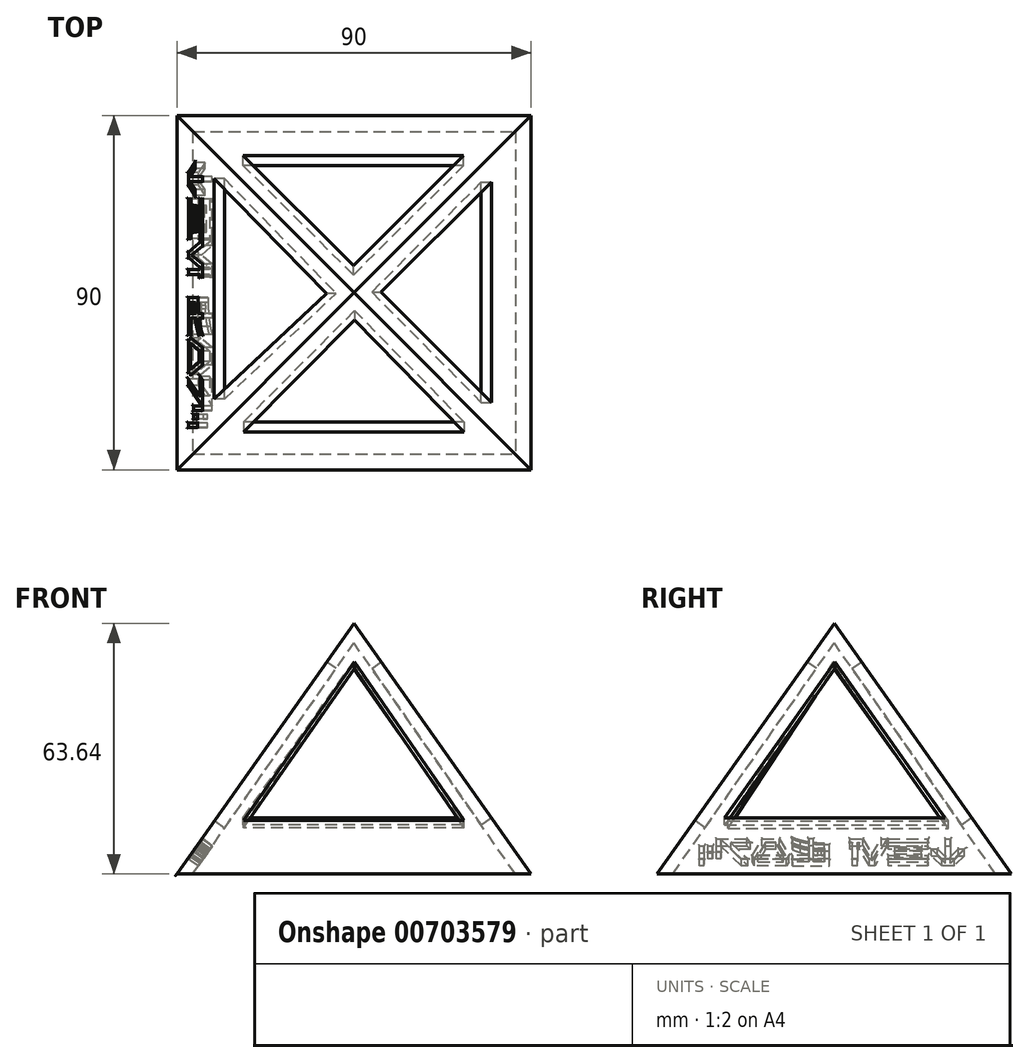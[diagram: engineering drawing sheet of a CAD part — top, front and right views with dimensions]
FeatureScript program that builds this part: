
annotation { "Feature Type Name" : "Feature", "Feature Type Description" : "" }
export const myFeature = defineFeature(function(context is Context, id is Id, definition is map)
    precondition{}
    {
        {
            var Q0;
            Q0=qCreatedBy(makeId("Top.planeOp"),FACE);
            cPlane(context, id + "F0", {"entities" : qUnion([Q0]), "cplaneType" : CPlaneType.OFFSET, "offset" : 63.64 * mm, "width" : 150 * mm, "height" : 150 * mm});
        }
        {
            var Q0;
            Q0=qCreatedBy(id+"F0.planeOp",FACE);
            var sketch = newSketch(context, id + "F1", { "sketchPlane" : qUnion([Q0])});
            skPoint(sketch, "E0", {"position": v(0, 0) * mm});
            skSolve(sketch);
        }
        {
            var Q0;
            Q0=qCreatedBy(makeId("Top.planeOp"),FACE);
            var sketch = newSketch(context, id + "F2", { "sketchPlane" : qUnion([Q0])});
            skLineSegment(sketch, "E1.bottom", {"start": v(-45, 45) * mm, "end": v(45, 45) * mm});
            skLineSegment(sketch, "E1.top", {"start": v(-45, -45) * mm, "end": v(45, -45) * mm});
            skLineSegment(sketch, "E1.left", {"start": v(-45, 45) * mm, "end": v(-45, -45) * mm});
            skLineSegment(sketch, "E1.right", {"start": v(45, 45) * mm, "end": v(45, -45) * mm});
            skPoint(sketch, "E2.orphan", {"position": v(-45, 0) * mm});
            skPoint(sketch, "E3.start.orphan", {"position": v(45, 0) * mm});
            skPoint(sketch, "E4.end.orphan", {"position": v(0, -45) * mm});
            skPoint(sketch, "E4.start.orphan", {"position": v(0, 45) * mm});
            skSolve(sketch);
        }
        {
            var Q0;
            Q0=makeQuery(id+"F2.imprint","IMPRINT",FACE,{"disambiguationData":[TD([[makeQuery(id+"F2.imprint","IMPRINT",EDGE,{"derivedFrom":sQuery(id+"F2.wireOp",EDGE,"E1.bottom")}),-1.0]])]});
            var Q1;
            Q1=sQuery(id+"F1.wireOp",VERTEX,"E0");
            loft(context, id + "F3", {"sheetProfilesArray" : [{ "sheetProfileEntities" : qUnion([Q0]) }, { "sheetProfileEntities" : qUnion([Q1]) }]});
        }
        {
            var Q0;
            Q0=qCreatedBy(makeId("Top.planeOp"),FACE);
            cPlane(context, id + "F4", {"entities" : qUnion([Q0]), "cplaneType" : CPlaneType.OFFSET, "offset" : 58.64 * mm, "width" : 150 * mm, "height" : 150 * mm});
        }
        {
            var Q0;
            Q0=qCreatedBy(id+"F4.planeOp",FACE);
            var sketch = newSketch(context, id + "F5", { "sketchPlane" : qUnion([Q0])});
            skPoint(sketch, "E5", {"position": v(0, 0) * mm});
            skSolve(sketch);
        }
        {
            var Q0;
            Q0=makeQuery(id+"F2.imprint","IMPRINT",FACE,{"disambiguationData":[TD([[makeQuery(id+"F2.imprint","IMPRINT",EDGE,{"derivedFrom":sQuery(id+"F2.wireOp",EDGE,"E1.bottom")}),-1.0]])]});
            var sketch = newSketch(context, id + "F6", { "sketchPlane" : qUnion([Q0])});
            skLineSegment(sketch, "E6.0", {"start": v(-41, 41) * mm, "end": v(-41, -41) * mm});
            skLineSegment(sketch, "E6.1", {"start": v(-41, 41) * mm, "end": v(41, 41) * mm});
            skLineSegment(sketch, "E6.2", {"start": v(41, 41) * mm, "end": v(41, -41) * mm});
            skLineSegment(sketch, "E6.3", {"start": v(-41, -41) * mm, "end": v(41, -41) * mm});
            skSolve(sketch);
        }
        {
            var Q1;
            Q1=makeQuery(id+"F6.imprint","IMPRINT",FACE,{"disambiguationData":[TD([[makeQuery(id+"F6.imprint","IMPRINT",EDGE,{"derivedFrom":sQuery(id+"F6.wireOp",EDGE,"E6.0")}),1.0]])]});
            var Q2;
            Q2=sQuery(id+"F5.wireOp",VERTEX,"E5");
            loft(context, id + "F7", {"operationType" : NewBodyOperationType.REMOVE, "sheetProfilesArray" : [{ "sheetProfileEntities" : qUnion([Q1]) }, { "sheetProfileEntities" : qUnion([Q2]) }]});
        }
        {
            var Q0;
            Q0=makeQuery(id+"F3.opLoft","SWEPT_FACE",FACE,{"disambiguationData":[OSD([sQuery(id+"F2.wireOp",EDGE,"E1.bottom"),sQuery(id+"F2.wireOp",EDGE,"E1.top"),sQuery(id+"F2.wireOp",EDGE,"E1.right")])]});
            var sketch = newSketch(context, id + "F8", { "sketchPlane" : qUnion([Q0])});
            skLineSegment(sketch, "E7.0", {"start": v(-27.83, -8.5) * mm, "end": v(0.15, 39.96) * mm});
            skLineSegment(sketch, "E7.1", {"start": v(28.13, -8.5) * mm, "end": v(0.15, 39.96) * mm});
            skLineSegment(sketch, "E8.0", {"start": v(28.13, -8.5) * mm, "end": v(-27.83, -8.5) * mm});
            skLineSegment(sketch, "E9", {"start": v(0, 51.96) * mm, "end": v(0.15, 39.96) * mm});
            skSolve(sketch);
        }
        {
            var Q0;
            Q0=makeQuery(id+"F3.opLoft","SWEPT_FACE",FACE,{"disambiguationData":[OSD([sQuery(id+"F2.wireOp",EDGE,"E1.bottom"),sQuery(id+"F2.wireOp",EDGE,"E1.left"),sQuery(id+"F2.wireOp",EDGE,"E1.right")])]});
            var sketch = newSketch(context, id + "F9", { "sketchPlane" : qUnion([Q0])});
            skLineSegment(sketch, "E10.0", {"start": v(-27.84, -8.5) * mm, "end": v(0.15, 39.96) * mm});
            skLineSegment(sketch, "E10.1", {"start": v(28.13, -8.5) * mm, "end": v(0.15, 39.96) * mm});
            skLineSegment(sketch, "E11.0", {"start": v(28.13, -8.5) * mm, "end": v(-27.84, -8.5) * mm});
            skLineSegment(sketch, "E12", {"start": v(0, 51.96) * mm, "end": v(0.15, 39.96) * mm});
            skSolve(sketch);
        }
        {
            var Q0;
            Q0=makeQuery(id+"F3.opLoft","SWEPT_FACE",FACE,{"disambiguationData":[OSD([sQuery(id+"F2.wireOp",EDGE,"E1.bottom"),sQuery(id+"F2.wireOp",EDGE,"E1.top"),sQuery(id+"F2.wireOp",EDGE,"E1.left")])]});
            var sketch = newSketch(context, id + "F10", { "sketchPlane" : qUnion([Q0])});
            skLineSegment(sketch, "E13.0", {"start": v(-28.98, -9.51) * mm, "end": v(0.15, 39.96) * mm});
            skLineSegment(sketch, "E13.1", {"start": v(26.99, -9.51) * mm, "end": v(0.15, 39.96) * mm});
            skLineSegment(sketch, "E14.0", {"start": v(26.99, -9.51) * mm, "end": v(-28.98, -9.51) * mm});
            skLineSegment(sketch, "E15", {"start": v(0, 51.96) * mm, "end": v(0.15, 39.96) * mm});
            skSolve(sketch);
        }
        {
            var Q0;
            Q0=makeQuery(id+"F3.opLoft","SWEPT_FACE",FACE,{"disambiguationData":[OSD([sQuery(id+"F2.wireOp",EDGE,"E1.top"),sQuery(id+"F2.wireOp",EDGE,"E1.left"),sQuery(id+"F2.wireOp",EDGE,"E1.right")])]});
            var sketch = newSketch(context, id + "F11", { "sketchPlane" : qUnion([Q0])});
            skLineSegment(sketch, "E16.0", {"start": v(-28.04, -9.4) * mm, "end": v(0.15, 39.96) * mm});
            skLineSegment(sketch, "E16.1", {"start": v(27.93, -9.4) * mm, "end": v(0.15, 39.96) * mm});
            skLineSegment(sketch, "E17.0", {"start": v(27.93, -9.4) * mm, "end": v(-28.04, -9.4) * mm});
            skLineSegment(sketch, "E18", {"start": v(0, 51.96) * mm, "end": v(0.15, 39.96) * mm});
            skSolve(sketch);
        }
        {
            var Q0;
            Q0=makeQuery(id+"F8.imprint","IMPRINT",FACE,{"disambiguationData":[TD([[makeQuery(id+"F8.imprint","IMPRINT",EDGE,{"derivedFrom":sQuery(id+"F8.wireOp",EDGE,"E7.0")}),-1.0]])]});
            extrude(context, id + "F12", {"entities" : qUnion([Q0]), "operationType" : NewBodyOperationType.REMOVE, "endBound" : BoundingType.SYMMETRIC, "oppositeDirection" : true, "depth" : 10 * mm, "offsetDistance" : 25 * mm});
        }
        {
            var Q0;
            Q0=makeQuery(id+"F9.imprint","IMPRINT",FACE,{"disambiguationData":[TD([[makeQuery(id+"F9.imprint","IMPRINT",EDGE,{"derivedFrom":sQuery(id+"F9.wireOp",EDGE,"E10.0")}),-1.0]])]});
            extrude(context, id + "F13", {"entities" : qUnion([Q0]), "operationType" : NewBodyOperationType.REMOVE, "oppositeDirection" : true, "depth" : 10.1 * mm, "offsetDistance" : 25 * mm});
        }
        {
            var Q0;
            Q0=makeQuery(id+"F10.imprint","IMPRINT",FACE,{"disambiguationData":[TD([[makeQuery(id+"F10.imprint","IMPRINT",EDGE,{"derivedFrom":sQuery(id+"F10.wireOp",EDGE,"E13.0")}),-1.0]])]});
            extrude(context, id + "F14", {"entities" : qUnion([Q0]), "operationType" : NewBodyOperationType.REMOVE, "oppositeDirection" : true, "depth" : 10 * mm, "offsetDistance" : 25 * mm});
        }
        {
            var Q0;
            Q0=makeQuery(id+"F11.imprint","IMPRINT",FACE,{"disambiguationData":[TD([[makeQuery(id+"F11.imprint","IMPRINT",EDGE,{"derivedFrom":sQuery(id+"F11.wireOp",EDGE,"E16.0")}),-1.0]])]});
            extrude(context, id + "F15", {"entities" : qUnion([Q0]), "operationType" : NewBodyOperationType.REMOVE, "oppositeDirection" : true, "depth" : 10 * mm, "offsetDistance" : 25 * mm});
        }
        {
            var Q0;
            Q0=makeQuery(id+"F3.opLoft","SWEPT_FACE",FACE,{"disambiguationData":[OSD([sQuery(id+"F2.wireOp",EDGE,"E1.bottom"),sQuery(id+"F2.wireOp",EDGE,"E1.top"),sQuery(id+"F2.wireOp",EDGE,"E1.left")])]});
            var sketch = newSketch(context, id + "F16", { "sketchPlane" : qUnion([Q0])});
            skLineSegment(sketch, "E19", {"start": v(-30.48, -21.2) * mm, "end": v(-27.31, -21.2) * mm});
            skLineSegment(sketch, "E20", {"start": v(-27.31, -21.2) * mm, "end": v(-24.66, -18.07) * mm});
            skLineSegment(sketch, "E21", {"start": v(-24.66, -18.07) * mm, "end": v(-26.25, -18.07) * mm});
            skLineSegment(sketch, "E22", {"start": v(-26.25, -18.07) * mm, "end": v(-28.3, -20.5) * mm});
            skLineSegment(sketch, "E23", {"start": v(-28.3, -20.5) * mm, "end": v(-28.3, -14.95) * mm});
            skLineSegment(sketch, "E24", {"start": v(-28.3, -14.95) * mm, "end": v(-29.48, -14.95) * mm});
            skLineSegment(sketch, "E25", {"start": v(-29.48, -14.95) * mm, "end": v(-29.48, -20.5) * mm});
            skLineSegment(sketch, "E26", {"start": v(-29.48, -20.5) * mm, "end": v(-31.54, -18.07) * mm});
            skLineSegment(sketch, "E27", {"start": v(-31.54, -18.07) * mm, "end": v(-33.13, -18.07) * mm});
            skLineSegment(sketch, "E28", {"start": v(-33.13, -18.07) * mm, "end": v(-30.48, -21.2) * mm});
            skLineSegment(sketch, "E29", {"start": v(-13.74, -16.13) * mm, "end": v(-13.74, -14.95) * mm});
            skLineSegment(sketch, "E30", {"start": v(-13.74, -14.95) * mm, "end": v(-23.85, -14.95) * mm});
            skLineSegment(sketch, "E31", {"start": v(-23.85, -14.95) * mm, "end": v(-23.85, -16.13) * mm});
            skLineSegment(sketch, "E32", {"start": v(-23.85, -16.13) * mm, "end": v(-13.74, -16.13) * mm});
            skLineSegment(sketch, "E33", {"start": v(-13.74, -21.2) * mm, "end": v(-13.74, -20.01) * mm});
            skLineSegment(sketch, "E34", {"start": v(-13.74, -20.01) * mm, "end": v(-23.85, -20.01) * mm});
            skLineSegment(sketch, "E35", {"start": v(-23.85, -20.01) * mm, "end": v(-23.85, -21.2) * mm});
            skLineSegment(sketch, "E36", {"start": v(-23.85, -21.2) * mm, "end": v(-13.74, -21.2) * mm});
            skLineSegment(sketch, "E37", {"start": v(-15.46, -18.66) * mm, "end": v(-15.46, -17.48) * mm});
            skLineSegment(sketch, "E38", {"start": v(-15.46, -17.48) * mm, "end": v(-22.13, -17.48) * mm});
            skLineSegment(sketch, "E39", {"start": v(-22.13, -17.48) * mm, "end": v(-22.13, -18.66) * mm});
            skLineSegment(sketch, "E40", {"start": v(-22.13, -18.66) * mm, "end": v(-15.46, -18.66) * mm});
            skLineSegment(sketch, "E41", {"start": v(-9.62, -19.72) * mm, "end": v(-11.96, -14.95) * mm});
            skLineSegment(sketch, "E42", {"start": v(-11.96, -14.95) * mm, "end": v(-13.4, -14.95) * mm});
            skLineSegment(sketch, "E43", {"start": v(-13.4, -14.95) * mm, "end": v(-10.33, -21.2) * mm});
            skLineSegment(sketch, "E44", {"start": v(-10.33, -21.2) * mm, "end": v(-8.9, -21.2) * mm});
            skLineSegment(sketch, "E45", {"start": v(-8.9, -21.2) * mm, "end": v(-6.42, -16.13) * mm});
            skLineSegment(sketch, "E46", {"start": v(-6.42, -16.13) * mm, "end": v(-5.84, -16.13) * mm});
            skLineSegment(sketch, "E47", {"start": v(-5.84, -16.13) * mm, "end": v(-5.84, -21.2) * mm});
            skLineSegment(sketch, "E48", {"start": v(-5.84, -21.2) * mm, "end": v(-4.66, -21.2) * mm});
            skLineSegment(sketch, "E49", {"start": v(-4.66, -21.2) * mm, "end": v(-4.66, -16.13) * mm});
            skLineSegment(sketch, "E50", {"start": v(-4.66, -16.13) * mm, "end": v(-3.94, -16.13) * mm});
            skLineSegment(sketch, "E51", {"start": v(-3.94, -16.13) * mm, "end": v(-3.94, -14.95) * mm});
            skLineSegment(sketch, "E52", {"start": v(-3.94, -14.95) * mm, "end": v(-7.28, -14.95) * mm});
            skLineSegment(sketch, "E53", {"start": v(-7.28, -14.95) * mm, "end": v(-9.62, -19.72) * mm});
            skLineSegment(sketch, "E54", {"start": v(2.43, -20.01) * mm, "end": v(5.3, -20.01) * mm});
            skLineSegment(sketch, "E55", {"start": v(5.3, -20.01) * mm, "end": v(5.3, -17.82) * mm});
            skLineSegment(sketch, "E56", {"start": v(2.43, -17.95) * mm, "end": v(2.43, -20.01) * mm});
            skLineSegment(sketch, "E57", {"start": v(5.3, -16.6) * mm, "end": v(5.3, -14.95) * mm});
            skLineSegment(sketch, "E58", {"start": v(5.3, -14.95) * mm, "end": v(6.48, -14.95) * mm});
            skLineSegment(sketch, "E59", {"start": v(6.48, -14.95) * mm, "end": v(6.48, -16.4) * mm});
            skLineSegment(sketch, "E60", {"start": v(10.66, -14.95) * mm, "end": v(10.66, -16.14) * mm});
            skLineSegment(sketch, "E61", {"start": v(6.48, -17.65) * mm, "end": v(6.48, -20.01) * mm});
            skLineSegment(sketch, "E62", {"start": v(6.48, -20.01) * mm, "end": v(10.66, -20.01) * mm});
            skLineSegment(sketch, "E63", {"start": v(10.66, -20.01) * mm, "end": v(10.66, -21.2) * mm});
            skLineSegment(sketch, "E64", {"start": v(10.66, -21.2) * mm, "end": v(1.25, -21.2) * mm});
            skLineSegment(sketch, "E65", {"start": v(1.25, -21.2) * mm, "end": v(1.25, -16.76) * mm});
            skLineSegment(sketch, "E66", {"start": v(1.25, -16.76) * mm, "end": v(2.43, -16.76) * mm});
            skLineSegment(sketch, "E67", {"start": v(12.92, -20.01) * mm, "end": v(14.82, -16.13) * mm});
            skLineSegment(sketch, "E68", {"start": v(14.82, -16.13) * mm, "end": v(17.48, -16.13) * mm});
            skLineSegment(sketch, "E69", {"start": v(17.48, -16.13) * mm, "end": v(19.37, -20.01) * mm});
            skLineSegment(sketch, "E70", {"start": v(19.37, -20.01) * mm, "end": v(12.92, -20.01) * mm});
            skLineSegment(sketch, "E71", {"start": v(20.26, -21.2) * mm, "end": v(20.83, -20.04) * mm});
            skLineSegment(sketch, "E72", {"start": v(20.83, -20.04) * mm, "end": v(18.33, -14.95) * mm});
            skLineSegment(sketch, "E73", {"start": v(18.33, -14.95) * mm, "end": v(13.96, -14.95) * mm});
            skLineSegment(sketch, "E74", {"start": v(13.96, -14.95) * mm, "end": v(11.5, -19.98) * mm});
            skLineSegment(sketch, "E75", {"start": v(11.5, -19.98) * mm, "end": v(12.09, -21.2) * mm});
            skLineSegment(sketch, "E76", {"start": v(12.09, -21.2) * mm, "end": v(20.26, -21.2) * mm});
            skLineSegment(sketch, "E77", {"start": v(23.56, -21.2) * mm, "end": v(28.74, -15.1) * mm});
            skLineSegment(sketch, "E78", {"start": v(28.86, -14.95) * mm, "end": v(22.22, -14.95) * mm});
            skLineSegment(sketch, "E79", {"start": v(22.22, -14.95) * mm, "end": v(21.22, -16.13) * mm});
            skLineSegment(sketch, "E80", {"start": v(21.22, -16.13) * mm, "end": v(26.26, -16.13) * mm});
            skLineSegment(sketch, "E81", {"start": v(26.26, -16.13) * mm, "end": v(21.97, -21.2) * mm});
            skLineSegment(sketch, "E82", {"start": v(21.97, -21.2) * mm, "end": v(23.56, -21.2) * mm});
            skLineSegment(sketch, "E83", {"start": v(29.92, -19) * mm, "end": v(29.92, -14.95) * mm});
            skLineSegment(sketch, "E84", {"start": v(29.92, -14.95) * mm, "end": v(28.74, -14.95) * mm});
            skLineSegment(sketch, "E85", {"start": v(28.74, -15.1) * mm, "end": v(28.74, -19) * mm});
            skLineSegment(sketch, "E86", {"start": v(28.74, -19) * mm, "end": v(29.92, -19) * mm});
            skLineSegment(sketch, "E87", {"start": v(34.22, -21.2) * mm, "end": v(34.22, -17.13) * mm});
            skLineSegment(sketch, "E88", {"start": v(34.22, -17.13) * mm, "end": v(33.04, -17.13) * mm});
            skLineSegment(sketch, "E89", {"start": v(33.04, -17.13) * mm, "end": v(33.04, -21.2) * mm});
            skLineSegment(sketch, "E90", {"start": v(33.04, -21.2) * mm, "end": v(34.22, -21.2) * mm});
            skLineSegment(sketch, "E91", {"start": v(32.07, -19) * mm, "end": v(32.07, -17.13) * mm});
            skLineSegment(sketch, "E92", {"start": v(32.07, -17.13) * mm, "end": v(30.89, -17.13) * mm});
            skLineSegment(sketch, "E93", {"start": v(30.89, -17.13) * mm, "end": v(30.89, -19) * mm});
            skLineSegment(sketch, "E94", {"start": v(30.89, -19) * mm, "end": v(32.07, -19) * mm});
            skFitSpline(sketch, "E95", {"points": [v(5.3, -17.82) * mm, v(5.1, -17.85) * mm, v(4.72, -17.9) * mm, v(4.34, -17.92) * mm, v(4.16, -17.93) * mm]});
            skFitSpline(sketch, "E96", {"points": [v(4.16, -17.93) * mm, v(4, -17.94) * mm, v(3.7, -17.95) * mm, v(3.4, -17.96) * mm, v(3.25, -17.96) * mm]});
            skFitSpline(sketch, "E97", {"points": [v(3.25, -17.96) * mm, v(3.1, -17.97) * mm, v(2.83, -17.97) * mm, v(2.56, -17.96) * mm, v(2.43, -17.95) * mm]});
            skFitSpline(sketch, "E98", {"points": [v(2.43, -16.76) * mm, v(2.56, -16.77) * mm, v(2.82, -16.78) * mm, v(3.1, -16.78) * mm, v(3.23, -16.77) * mm]});
            skFitSpline(sketch, "E99", {"points": [v(3.23, -16.77) * mm, v(3.37, -16.77) * mm, v(3.67, -16.76) * mm, v(3.98, -16.74) * mm, v(4.14, -16.73) * mm]});
            skFitSpline(sketch, "E100", {"points": [v(4.14, -16.73) * mm, v(4.33, -16.71) * mm, v(4.71, -16.68) * mm, v(5.1, -16.63) * mm, v(5.3, -16.6) * mm]});
            skFitSpline(sketch, "E101", {"points": [v(6.48, -16.4) * mm, v(6.81, -16.33) * mm, v(7.5, -16.18) * mm, v(8.18, -15.97) * mm, v(8.52, -15.86) * mm]});
            skFitSpline(sketch, "E102", {"points": [v(8.52, -15.86) * mm, v(8.88, -15.74) * mm, v(9.62, -15.48) * mm, v(10.3, -15.13) * mm, v(10.66, -14.95) * mm]});
            skFitSpline(sketch, "E103", {"points": [v(10.66, -16.14) * mm, v(10.33, -16.3) * mm, v(9.66, -16.64) * mm, v(8.96, -16.92) * mm, v(8.6, -17.05) * mm]});
            skFitSpline(sketch, "E104", {"points": [v(8.6, -17.05) * mm, v(8.25, -17.18) * mm, v(7.56, -17.42) * mm, v(6.84, -17.57) * mm, v(6.48, -17.65) * mm]});
            skSolve(sketch);
        }
        {
            var Q0;
            Q0=makeQuery(id+"F16.imprint","IMPRINT",FACE,{"disambiguationData":[TD([[makeQuery(id+"F16.imprint","IMPRINT",EDGE,{"derivedFrom":sQuery(id+"F16.wireOp",EDGE,"E19")}),1.0]])]});
            var Q1;
            Q1=makeQuery(id+"F16.imprint","IMPRINT",FACE,{"disambiguationData":[TD([[makeQuery(id+"F16.imprint","IMPRINT",EDGE,{"derivedFrom":sQuery(id+"F16.wireOp",EDGE,"E33")}),1.0]])]});
            var Q2;
            Q2=makeQuery(id+"F16.imprint","IMPRINT",FACE,{"disambiguationData":[TD([[makeQuery(id+"F16.imprint","IMPRINT",EDGE,{"derivedFrom":sQuery(id+"F16.wireOp",EDGE,"E37")}),1.0]])]});
            var Q3;
            Q3=makeQuery(id+"F16.imprint","IMPRINT",FACE,{"disambiguationData":[TD([[makeQuery(id+"F16.imprint","IMPRINT",EDGE,{"derivedFrom":sQuery(id+"F16.wireOp",EDGE,"E29")}),1.0]])]});
            var Q4;
            Q4=makeQuery(id+"F16.imprint","IMPRINT",FACE,{"disambiguationData":[TD([[makeQuery(id+"F16.imprint","IMPRINT",EDGE,{"derivedFrom":sQuery(id+"F16.wireOp",EDGE,"E41")}),1.0]])]});
            var Q5;
            Q5=makeQuery(id+"F16.imprint","IMPRINT",FACE,{"disambiguationData":[TD([[makeQuery(id+"F16.imprint","IMPRINT",EDGE,{"derivedFrom":sQuery(id+"F16.wireOp",EDGE,"E54")}),-1.0]])]});
            var Q6;
            Q6=makeQuery(id+"F16.imprint","IMPRINT",FACE,{"disambiguationData":[TD([[makeQuery(id+"F16.imprint","IMPRINT",EDGE,{"derivedFrom":sQuery(id+"F16.wireOp",EDGE,"E67")}),1.0]])]});
            var Q7;
            Q7=makeQuery(id+"F16.imprint","IMPRINT",FACE,{"disambiguationData":[TD([[makeQuery(id+"F16.imprint","IMPRINT",EDGE,{"derivedFrom":sQuery(id+"F16.wireOp",EDGE,"E77")}),1.0]])]});
            var Q8;
            Q8=makeQuery(id+"F16.imprint","IMPRINT",FACE,{"disambiguationData":[TD([[makeQuery(id+"F16.imprint","IMPRINT",EDGE,{"derivedFrom":sQuery(id+"F16.wireOp",EDGE,"E91")}),1.0]])]});
            var Q9;
            Q9=makeQuery(id+"F16.imprint","IMPRINT",FACE,{"disambiguationData":[TD([[makeQuery(id+"F16.imprint","IMPRINT",EDGE,{"derivedFrom":sQuery(id+"F16.wireOp",EDGE,"E87")}),1.0]])]});
            extrude(context, id + "F17", {"entities" : qUnion([Q0, Q1, Q2, Q3, Q4, Q5, Q6, Q7, Q8, Q9]), "operationType" : NewBodyOperationType.REMOVE, "oppositeDirection" : true, "depth" : 9 * mm, "offsetDistance" : 25 * mm, "hasSecondDirection" : true, "secondDirectionOppositeDirection" : true, "secondDirectionDepth" : .3 * mm});
        }
        {
            var Q0;
            Q0=makeQuery(id+"F16.imprint","IMPRINT",FACE,{"disambiguationData":[TD([[makeQuery(id+"F16.imprint","IMPRINT",EDGE,{"derivedFrom":sQuery(id+"F16.wireOp",EDGE,"E19")}),1.0]])]});
            var Q1;
            Q1=makeQuery(id+"F16.imprint","IMPRINT",FACE,{"disambiguationData":[TD([[makeQuery(id+"F16.imprint","IMPRINT",EDGE,{"derivedFrom":sQuery(id+"F16.wireOp",EDGE,"E37")}),1.0]])]});
            var Q2;
            Q2=makeQuery(id+"F16.imprint","IMPRINT",FACE,{"disambiguationData":[TD([[makeQuery(id+"F16.imprint","IMPRINT",EDGE,{"derivedFrom":sQuery(id+"F16.wireOp",EDGE,"E33")}),1.0]])]});
            var Q3;
            Q3=makeQuery(id+"F16.imprint","IMPRINT",FACE,{"disambiguationData":[TD([[makeQuery(id+"F16.imprint","IMPRINT",EDGE,{"derivedFrom":sQuery(id+"F16.wireOp",EDGE,"E29")}),1.0]])]});
            var Q4;
            Q4=makeQuery(id+"F16.imprint","IMPRINT",FACE,{"disambiguationData":[TD([[makeQuery(id+"F16.imprint","IMPRINT",EDGE,{"derivedFrom":sQuery(id+"F16.wireOp",EDGE,"E41")}),1.0]])]});
            var Q5;
            Q5=makeQuery(id+"F16.imprint","IMPRINT",FACE,{"disambiguationData":[TD([[makeQuery(id+"F16.imprint","IMPRINT",EDGE,{"derivedFrom":sQuery(id+"F16.wireOp",EDGE,"E54")}),-1.0]])]});
            var Q6;
            Q6=makeQuery(id+"F16.imprint","IMPRINT",FACE,{"disambiguationData":[TD([[makeQuery(id+"F16.imprint","IMPRINT",EDGE,{"derivedFrom":sQuery(id+"F16.wireOp",EDGE,"E67")}),1.0]])]});
            var Q7;
            Q7=makeQuery(id+"F16.imprint","IMPRINT",FACE,{"disambiguationData":[TD([[makeQuery(id+"F16.imprint","IMPRINT",EDGE,{"derivedFrom":sQuery(id+"F16.wireOp",EDGE,"E77")}),1.0]])]});
            var Q8;
            Q8=makeQuery(id+"F16.imprint","IMPRINT",FACE,{"disambiguationData":[TD([[makeQuery(id+"F16.imprint","IMPRINT",EDGE,{"derivedFrom":sQuery(id+"F16.wireOp",EDGE,"E91")}),1.0]])]});
            var Q9;
            Q9=makeQuery(id+"F16.imprint","IMPRINT",FACE,{"disambiguationData":[TD([[makeQuery(id+"F16.imprint","IMPRINT",EDGE,{"derivedFrom":sQuery(id+"F16.wireOp",EDGE,"E87")}),1.0]])]});
            extrude(context, id + "F18", {"entities" : qUnion([Q0, Q1, Q2, Q3, Q4, Q5, Q6, Q7, Q8, Q9]), "operationType" : NewBodyOperationType.REMOVE, "oppositeDirection" : true, "depth" : .2 * mm, "offsetDistance" : 25 * mm});
        }
        {
            var Q0;
            Q0=makeQuery(id+"F18.boolean.opBoolean","COPY",EDGE,{"derivedFrom":makeQuery(id+"F18.opExtrude","CAP_EDGE",EDGE,{"disambiguationData":[OSD([sQuery(id+"F16.wireOp",EDGE,"E21")])],"isStart":true})});
            var Q1;
            Q1=makeQuery(id+"F18.boolean.opBoolean","COPY",EDGE,{"derivedFrom":makeQuery(id+"F18.opExtrude","CAP_EDGE",EDGE,{"disambiguationData":[OSD([sQuery(id+"F16.wireOp",EDGE,"E20")])],"isStart":true})});
            var Q2;
            Q2=makeQuery(id+"F18.boolean.opBoolean","COPY",EDGE,{"derivedFrom":makeQuery(id+"F18.opExtrude","CAP_EDGE",EDGE,{"disambiguationData":[OSD([sQuery(id+"F16.wireOp",EDGE,"E23")])],"isStart":true})});
            var Q3;
            Q3=makeQuery(id+"F18.boolean.opBoolean","COPY",EDGE,{"derivedFrom":makeQuery(id+"F18.opExtrude","CAP_EDGE",EDGE,{"disambiguationData":[OSD([sQuery(id+"F16.wireOp",EDGE,"E24")])],"isStart":true})});
            var Q4;
            Q4=makeQuery(id+"F18.boolean.opBoolean","COPY",EDGE,{"derivedFrom":makeQuery(id+"F18.opExtrude","CAP_EDGE",EDGE,{"disambiguationData":[OSD([sQuery(id+"F16.wireOp",EDGE,"E25")])],"isStart":true})});
            var Q5;
            Q5=makeQuery(id+"F18.boolean.opBoolean","COPY",EDGE,{"derivedFrom":makeQuery(id+"F18.opExtrude","CAP_EDGE",EDGE,{"disambiguationData":[OSD([sQuery(id+"F16.wireOp",EDGE,"E26")])],"isStart":true})});
            var Q6;
            Q6=makeQuery(id+"F18.boolean.opBoolean","COPY",EDGE,{"derivedFrom":makeQuery(id+"F18.opExtrude","CAP_EDGE",EDGE,{"disambiguationData":[OSD([sQuery(id+"F16.wireOp",EDGE,"E27")])],"isStart":true})});
            var Q7;
            Q7=makeQuery(id+"F18.boolean.opBoolean","COPY",EDGE,{"derivedFrom":makeQuery(id+"F18.opExtrude","CAP_EDGE",EDGE,{"disambiguationData":[OSD([sQuery(id+"F16.wireOp",EDGE,"E28")])],"isStart":true})});
            var Q8;
            Q8=makeQuery(id+"F18.boolean.opBoolean","COPY",EDGE,{"derivedFrom":makeQuery(id+"F18.opExtrude","CAP_EDGE",EDGE,{"disambiguationData":[OSD([sQuery(id+"F16.wireOp",EDGE,"E19")])],"isStart":true})});
            var Q9;
            Q9=makeQuery(id+"F18.boolean.opBoolean","COPY",EDGE,{"derivedFrom":makeQuery(id+"F18.opExtrude","CAP_EDGE",EDGE,{"disambiguationData":[OSD([sQuery(id+"F16.wireOp",EDGE,"E22")])],"isStart":true})});
            var Q10;
            Q10=makeQuery(id+"F18.boolean.opBoolean","COPY",EDGE,{"derivedFrom":makeQuery(id+"F18.opExtrude","CAP_EDGE",EDGE,{"disambiguationData":[OSD([sQuery(id+"F16.wireOp",EDGE,"E30")])],"isStart":true})});
            var Q11;
            Q11=makeQuery(id+"F18.boolean.opBoolean","COPY",EDGE,{"derivedFrom":makeQuery(id+"F18.opExtrude","CAP_EDGE",EDGE,{"disambiguationData":[OSD([sQuery(id+"F16.wireOp",EDGE,"E31")])],"isStart":true})});
            var Q12;
            Q12=makeQuery(id+"F18.boolean.opBoolean","COPY",EDGE,{"derivedFrom":makeQuery(id+"F18.opExtrude","CAP_EDGE",EDGE,{"disambiguationData":[OSD([sQuery(id+"F16.wireOp",EDGE,"E29")])],"isStart":true})});
            var Q13;
            Q13=makeQuery(id+"F18.boolean.opBoolean","COPY",EDGE,{"derivedFrom":makeQuery(id+"F18.opExtrude","CAP_EDGE",EDGE,{"disambiguationData":[OSD([sQuery(id+"F16.wireOp",EDGE,"E32")])],"isStart":true})});
            var Q14;
            Q14=makeQuery(id+"F18.boolean.opBoolean","COPY",EDGE,{"derivedFrom":makeQuery(id+"F18.opExtrude","CAP_EDGE",EDGE,{"disambiguationData":[OSD([sQuery(id+"F16.wireOp",EDGE,"E42")])],"isStart":true})});
            var Q15;
            Q15=makeQuery(id+"F18.boolean.opBoolean","COPY",EDGE,{"derivedFrom":makeQuery(id+"F18.opExtrude","CAP_EDGE",EDGE,{"disambiguationData":[OSD([sQuery(id+"F16.wireOp",EDGE,"E38")])],"isStart":true})});
            var Q16;
            Q16=makeQuery(id+"F18.boolean.opBoolean","COPY",EDGE,{"derivedFrom":makeQuery(id+"F18.opExtrude","CAP_EDGE",EDGE,{"disambiguationData":[OSD([sQuery(id+"F16.wireOp",EDGE,"E39")])],"isStart":true})});
            var Q17;
            Q17=makeQuery(id+"F18.boolean.opBoolean","COPY",EDGE,{"derivedFrom":makeQuery(id+"F18.opExtrude","CAP_EDGE",EDGE,{"disambiguationData":[OSD([sQuery(id+"F16.wireOp",EDGE,"E40")])],"isStart":true})});
            var Q18;
            Q18=makeQuery(id+"F18.boolean.opBoolean","COPY",EDGE,{"derivedFrom":makeQuery(id+"F18.opExtrude","CAP_EDGE",EDGE,{"disambiguationData":[OSD([sQuery(id+"F16.wireOp",EDGE,"E37")])],"isStart":true})});
            var Q19;
            Q19=makeQuery(id+"F18.boolean.opBoolean","COPY",EDGE,{"derivedFrom":makeQuery(id+"F18.opExtrude","CAP_EDGE",EDGE,{"disambiguationData":[OSD([sQuery(id+"F16.wireOp",EDGE,"E34")])],"isStart":true})});
            var Q20;
            Q20=makeQuery(id+"F18.boolean.opBoolean","COPY",EDGE,{"derivedFrom":makeQuery(id+"F18.opExtrude","CAP_EDGE",EDGE,{"disambiguationData":[OSD([sQuery(id+"F16.wireOp",EDGE,"E33")])],"isStart":true})});
            var Q21;
            Q21=makeQuery(id+"F18.boolean.opBoolean","COPY",EDGE,{"derivedFrom":makeQuery(id+"F18.opExtrude","CAP_EDGE",EDGE,{"disambiguationData":[OSD([sQuery(id+"F16.wireOp",EDGE,"E36")])],"isStart":true})});
            var Q22;
            Q22=makeQuery(id+"F18.boolean.opBoolean","COPY",EDGE,{"derivedFrom":makeQuery(id+"F18.opExtrude","CAP_EDGE",EDGE,{"disambiguationData":[OSD([sQuery(id+"F16.wireOp",EDGE,"E35")])],"isStart":true})});
            var Q23;
            Q23=makeQuery(id+"F18.boolean.opBoolean","COPY",EDGE,{"derivedFrom":makeQuery(id+"F18.opExtrude","CAP_EDGE",EDGE,{"disambiguationData":[OSD([sQuery(id+"F16.wireOp",EDGE,"E41")])],"isStart":true})});
            var Q24;
            Q24=makeQuery(id+"F18.boolean.opBoolean","COPY",EDGE,{"derivedFrom":makeQuery(id+"F18.opExtrude","CAP_EDGE",EDGE,{"disambiguationData":[OSD([sQuery(id+"F16.wireOp",EDGE,"E43")])],"isStart":true})});
            var Q25;
            Q25=makeQuery(id+"F18.boolean.opBoolean","COPY",EDGE,{"derivedFrom":makeQuery(id+"F18.opExtrude","CAP_EDGE",EDGE,{"disambiguationData":[OSD([sQuery(id+"F16.wireOp",EDGE,"E53")])],"isStart":true})});
            var Q26;
            Q26=makeQuery(id+"F18.boolean.opBoolean","COPY",EDGE,{"derivedFrom":makeQuery(id+"F18.opExtrude","CAP_EDGE",EDGE,{"disambiguationData":[OSD([sQuery(id+"F16.wireOp",EDGE,"E52")])],"isStart":true})});
            var Q27;
            Q27=makeQuery(id+"F18.boolean.opBoolean","COPY",EDGE,{"derivedFrom":makeQuery(id+"F18.opExtrude","CAP_EDGE",EDGE,{"disambiguationData":[OSD([sQuery(id+"F16.wireOp",EDGE,"E51")])],"isStart":true})});
            var Q28;
            Q28=makeQuery(id+"F18.boolean.opBoolean","COPY",EDGE,{"derivedFrom":makeQuery(id+"F18.opExtrude","CAP_EDGE",EDGE,{"disambiguationData":[OSD([sQuery(id+"F16.wireOp",EDGE,"E49")])],"isStart":true})});
            var Q29;
            Q29=makeQuery(id+"F18.boolean.opBoolean","COPY",EDGE,{"derivedFrom":makeQuery(id+"F18.opExtrude","CAP_EDGE",EDGE,{"disambiguationData":[OSD([sQuery(id+"F16.wireOp",EDGE,"E48")])],"isStart":true})});
            var Q30;
            Q30=makeQuery(id+"F18.boolean.opBoolean","COPY",EDGE,{"derivedFrom":makeQuery(id+"F18.opExtrude","CAP_EDGE",EDGE,{"disambiguationData":[OSD([sQuery(id+"F16.wireOp",EDGE,"E47")])],"isStart":true})});
            var Q31;
            Q31=makeQuery(id+"F18.boolean.opBoolean","COPY",EDGE,{"derivedFrom":makeQuery(id+"F18.opExtrude","CAP_EDGE",EDGE,{"disambiguationData":[OSD([sQuery(id+"F16.wireOp",EDGE,"E45")])],"isStart":true})});
            var Q32;
            Q32=makeQuery(id+"F18.boolean.opBoolean","COPY",EDGE,{"derivedFrom":makeQuery(id+"F18.opExtrude","CAP_EDGE",EDGE,{"disambiguationData":[OSD([sQuery(id+"F16.wireOp",EDGE,"E44")])],"isStart":true})});
            var Q33;
            Q33=makeQuery(id+"F18.boolean.opBoolean","COPY",EDGE,{"derivedFrom":makeQuery(id+"F18.opExtrude","CAP_EDGE",EDGE,{"disambiguationData":[OSD([sQuery(id+"F16.wireOp",EDGE,"E100")])],"isStart":true})});
            var Q34;
            Q34=makeQuery(id+"F18.boolean.opBoolean","COPY",EDGE,{"derivedFrom":makeQuery(id+"F18.opExtrude","CAP_EDGE",EDGE,{"disambiguationData":[OSD([sQuery(id+"F16.wireOp",EDGE,"E99")])],"isStart":true})});
            var Q35;
            Q35=makeQuery(id+"F18.boolean.opBoolean","COPY",EDGE,{"derivedFrom":makeQuery(id+"F18.opExtrude","CAP_EDGE",EDGE,{"disambiguationData":[OSD([sQuery(id+"F16.wireOp",EDGE,"E98")])],"isStart":true})});
            var Q36;
            Q36=makeQuery(id+"F18.boolean.opBoolean","COPY",EDGE,{"derivedFrom":makeQuery(id+"F18.opExtrude","CAP_EDGE",EDGE,{"disambiguationData":[OSD([sQuery(id+"F16.wireOp",EDGE,"E65")])],"isStart":true})});
            var Q37;
            Q37=makeQuery(id+"F18.boolean.opBoolean","COPY",EDGE,{"derivedFrom":makeQuery(id+"F18.opExtrude","CAP_EDGE",EDGE,{"disambiguationData":[OSD([sQuery(id+"F16.wireOp",EDGE,"E58")])],"isStart":true})});
            var Q38;
            Q38=makeQuery(id+"F18.boolean.opBoolean","COPY",EDGE,{"derivedFrom":makeQuery(id+"F18.opExtrude","CAP_EDGE",EDGE,{"disambiguationData":[OSD([sQuery(id+"F16.wireOp",EDGE,"E57")])],"isStart":true})});
            var Q39;
            Q39=makeQuery(id+"F18.boolean.opBoolean","COPY",EDGE,{"derivedFrom":makeQuery(id+"F18.opExtrude","CAP_EDGE",EDGE,{"disambiguationData":[OSD([sQuery(id+"F16.wireOp",EDGE,"E59")])],"isStart":true})});
            var Q40;
            Q40=makeQuery(id+"F18.boolean.opBoolean","COPY",EDGE,{"derivedFrom":makeQuery(id+"F18.opExtrude","CAP_EDGE",EDGE,{"disambiguationData":[OSD([sQuery(id+"F16.wireOp",EDGE,"E101")])],"isStart":true})});
            var Q41;
            Q41=makeQuery(id+"F18.boolean.opBoolean","COPY",EDGE,{"derivedFrom":makeQuery(id+"F18.opExtrude","CAP_EDGE",EDGE,{"disambiguationData":[OSD([sQuery(id+"F16.wireOp",EDGE,"E102")])],"isStart":true})});
            var Q42;
            Q42=makeQuery(id+"F18.boolean.opBoolean","COPY",EDGE,{"derivedFrom":makeQuery(id+"F18.opExtrude","CAP_EDGE",EDGE,{"disambiguationData":[OSD([sQuery(id+"F16.wireOp",EDGE,"E60")])],"isStart":true})});
            var Q43;
            Q43=makeQuery(id+"F18.boolean.opBoolean","COPY",EDGE,{"derivedFrom":makeQuery(id+"F18.opExtrude","CAP_EDGE",EDGE,{"disambiguationData":[OSD([sQuery(id+"F16.wireOp",EDGE,"E103")])],"isStart":true})});
            var Q44;
            Q44=makeQuery(id+"F18.boolean.opBoolean","COPY",EDGE,{"derivedFrom":makeQuery(id+"F18.opExtrude","CAP_EDGE",EDGE,{"disambiguationData":[OSD([sQuery(id+"F16.wireOp",EDGE,"E104")])],"isStart":true})});
            var Q45;
            Q45=makeQuery(id+"F18.boolean.opBoolean","COPY",EDGE,{"derivedFrom":makeQuery(id+"F18.opExtrude","CAP_EDGE",EDGE,{"disambiguationData":[OSD([sQuery(id+"F16.wireOp",EDGE,"E61")])],"isStart":true})});
            var Q46;
            Q46=makeQuery(id+"F18.boolean.opBoolean","COPY",EDGE,{"derivedFrom":makeQuery(id+"F18.opExtrude","CAP_EDGE",EDGE,{"disambiguationData":[OSD([sQuery(id+"F16.wireOp",EDGE,"E62")])],"isStart":true})});
            var Q47;
            Q47=makeQuery(id+"F18.boolean.opBoolean","COPY",EDGE,{"derivedFrom":makeQuery(id+"F18.opExtrude","CAP_EDGE",EDGE,{"disambiguationData":[OSD([sQuery(id+"F16.wireOp",EDGE,"E63")])],"isStart":true})});
            var Q48;
            Q48=makeQuery(id+"F18.boolean.opBoolean","COPY",EDGE,{"derivedFrom":makeQuery(id+"F18.opExtrude","CAP_EDGE",EDGE,{"disambiguationData":[OSD([sQuery(id+"F16.wireOp",EDGE,"E64")])],"isStart":true})});
            var Q49;
            Q49=makeQuery(id+"F18.boolean.opBoolean","COPY",EDGE,{"derivedFrom":makeQuery(id+"F18.opExtrude","CAP_EDGE",EDGE,{"disambiguationData":[OSD([sQuery(id+"F16.wireOp",EDGE,"E54")])],"isStart":true})});
            var Q50;
            Q50=makeQuery(id+"F18.boolean.opBoolean","COPY",EDGE,{"derivedFrom":makeQuery(id+"F18.opExtrude","CAP_EDGE",EDGE,{"disambiguationData":[OSD([sQuery(id+"F16.wireOp",EDGE,"E56")])],"isStart":true})});
            var Q51;
            Q51=makeQuery(id+"F18.boolean.opBoolean","COPY",EDGE,{"derivedFrom":makeQuery(id+"F18.opExtrude","CAP_EDGE",EDGE,{"disambiguationData":[OSD([sQuery(id+"F16.wireOp",EDGE,"E97")])],"isStart":true})});
            var Q52;
            Q52=makeQuery(id+"F18.boolean.opBoolean","COPY",EDGE,{"derivedFrom":makeQuery(id+"F18.opExtrude","CAP_EDGE",EDGE,{"disambiguationData":[OSD([sQuery(id+"F16.wireOp",EDGE,"E55")])],"isStart":true})});
            var Q53;
            Q53=makeQuery(id+"F18.boolean.opBoolean","COPY",EDGE,{"derivedFrom":makeQuery(id+"F18.opExtrude","CAP_EDGE",EDGE,{"disambiguationData":[OSD([sQuery(id+"F16.wireOp",EDGE,"E73")])],"isStart":true})});
            var Q54;
            Q54=makeQuery(id+"F18.boolean.opBoolean","COPY",EDGE,{"derivedFrom":makeQuery(id+"F18.opExtrude","CAP_EDGE",EDGE,{"disambiguationData":[OSD([sQuery(id+"F16.wireOp",EDGE,"E74")])],"isStart":true})});
            var Q55;
            Q55=makeQuery(id+"F18.boolean.opBoolean","COPY",EDGE,{"derivedFrom":makeQuery(id+"F18.opExtrude","CAP_EDGE",EDGE,{"disambiguationData":[OSD([sQuery(id+"F16.wireOp",EDGE,"E72")])],"isStart":true})});
            var Q56;
            Q56=makeQuery(id+"F18.boolean.opBoolean","COPY",EDGE,{"derivedFrom":makeQuery(id+"F18.opExtrude","CAP_EDGE",EDGE,{"disambiguationData":[OSD([sQuery(id+"F16.wireOp",EDGE,"E67")])],"isStart":true})});
            var Q57;
            Q57=makeQuery(id+"F18.boolean.opBoolean","COPY",EDGE,{"derivedFrom":makeQuery(id+"F18.opExtrude","CAP_EDGE",EDGE,{"disambiguationData":[OSD([sQuery(id+"F16.wireOp",EDGE,"E68")])],"isStart":true})});
            var Q58;
            Q58=makeQuery(id+"F18.boolean.opBoolean","COPY",EDGE,{"derivedFrom":makeQuery(id+"F18.opExtrude","CAP_EDGE",EDGE,{"disambiguationData":[OSD([sQuery(id+"F16.wireOp",EDGE,"E69")])],"isStart":true})});
            var Q59;
            Q59=makeQuery(id+"F18.boolean.opBoolean","COPY",EDGE,{"derivedFrom":makeQuery(id+"F18.opExtrude","CAP_EDGE",EDGE,{"disambiguationData":[OSD([sQuery(id+"F16.wireOp",EDGE,"E75")])],"isStart":true})});
            var Q60;
            Q60=makeQuery(id+"F18.boolean.opBoolean","COPY",EDGE,{"derivedFrom":makeQuery(id+"F18.opExtrude","CAP_EDGE",EDGE,{"disambiguationData":[OSD([sQuery(id+"F16.wireOp",EDGE,"E70")])],"isStart":true})});
            var Q61;
            Q61=makeQuery(id+"F18.boolean.opBoolean","COPY",EDGE,{"derivedFrom":makeQuery(id+"F18.opExtrude","CAP_EDGE",EDGE,{"disambiguationData":[OSD([sQuery(id+"F16.wireOp",EDGE,"E76")])],"isStart":true})});
            var Q62;
            Q62=makeQuery(id+"F18.boolean.opBoolean","COPY",EDGE,{"derivedFrom":makeQuery(id+"F18.opExtrude","CAP_EDGE",EDGE,{"disambiguationData":[OSD([sQuery(id+"F16.wireOp",EDGE,"E71")])],"isStart":true})});
            var Q63;
            Q63=makeQuery(id+"F18.boolean.opBoolean","COPY",EDGE,{"derivedFrom":makeQuery(id+"F18.opExtrude","CAP_EDGE",EDGE,{"disambiguationData":[OSD([sQuery(id+"F16.wireOp",EDGE,"E79")])],"isStart":true})});
            var Q64;
            Q64=makeQuery(id+"F18.boolean.opBoolean","COPY",EDGE,{"derivedFrom":makeQuery(id+"F18.opExtrude","CAP_EDGE",EDGE,{"disambiguationData":[OSD([sQuery(id+"F16.wireOp",EDGE,"E78"),sQuery(id+"F16.wireOp",EDGE,"E84")])],"isStart":true})});
            var Q65;
            Q65=makeQuery(id+"F18.boolean.opBoolean","COPY",EDGE,{"derivedFrom":makeQuery(id+"F18.opExtrude","CAP_EDGE",EDGE,{"disambiguationData":[OSD([sQuery(id+"F16.wireOp",EDGE,"E80")])],"isStart":true})});
            var Q66;
            Q66=makeQuery(id+"F18.boolean.opBoolean","COPY",EDGE,{"derivedFrom":makeQuery(id+"F18.opExtrude","CAP_EDGE",EDGE,{"disambiguationData":[OSD([sQuery(id+"F16.wireOp",EDGE,"E81")])],"isStart":true})});
            var Q67;
            Q67=makeQuery(id+"F18.boolean.opBoolean","COPY",EDGE,{"derivedFrom":makeQuery(id+"F18.opExtrude","CAP_EDGE",EDGE,{"disambiguationData":[OSD([sQuery(id+"F16.wireOp",EDGE,"E82")])],"isStart":true})});
            var Q68;
            Q68=makeQuery(id+"F18.boolean.opBoolean","COPY",EDGE,{"derivedFrom":makeQuery(id+"F18.opExtrude","CAP_EDGE",EDGE,{"disambiguationData":[OSD([sQuery(id+"F16.wireOp",EDGE,"E77")])],"isStart":true})});
            var Q69;
            Q69=makeQuery(id+"F18.boolean.opBoolean","COPY",EDGE,{"derivedFrom":makeQuery(id+"F18.opExtrude","CAP_EDGE",EDGE,{"disambiguationData":[OSD([sQuery(id+"F16.wireOp",EDGE,"E85")])],"isStart":true})});
            var Q70;
            Q70=makeQuery(id+"F18.boolean.opBoolean","COPY",EDGE,{"derivedFrom":makeQuery(id+"F18.opExtrude","CAP_EDGE",EDGE,{"disambiguationData":[OSD([sQuery(id+"F16.wireOp",EDGE,"E86")])],"isStart":true})});
            var Q71;
            Q71=makeQuery(id+"F18.boolean.opBoolean","COPY",EDGE,{"derivedFrom":makeQuery(id+"F18.opExtrude","CAP_EDGE",EDGE,{"disambiguationData":[OSD([sQuery(id+"F16.wireOp",EDGE,"E83")])],"isStart":true})});
            var Q72;
            Q72=makeQuery(id+"F18.boolean.opBoolean","COPY",EDGE,{"derivedFrom":makeQuery(id+"F18.opExtrude","CAP_EDGE",EDGE,{"disambiguationData":[OSD([sQuery(id+"F16.wireOp",EDGE,"E92")])],"isStart":true})});
            var Q73;
            Q73=makeQuery(id+"F18.boolean.opBoolean","COPY",EDGE,{"derivedFrom":makeQuery(id+"F18.opExtrude","CAP_EDGE",EDGE,{"disambiguationData":[OSD([sQuery(id+"F16.wireOp",EDGE,"E91")])],"isStart":true})});
            var Q74;
            Q74=makeQuery(id+"F18.boolean.opBoolean","COPY",EDGE,{"derivedFrom":makeQuery(id+"F18.opExtrude","CAP_EDGE",EDGE,{"disambiguationData":[OSD([sQuery(id+"F16.wireOp",EDGE,"E94")])],"isStart":true})});
            var Q75;
            Q75=makeQuery(id+"F18.boolean.opBoolean","COPY",EDGE,{"derivedFrom":makeQuery(id+"F18.opExtrude","CAP_EDGE",EDGE,{"disambiguationData":[OSD([sQuery(id+"F16.wireOp",EDGE,"E93")])],"isStart":true})});
            var Q76;
            Q76=makeQuery(id+"F18.boolean.opBoolean","COPY",EDGE,{"derivedFrom":makeQuery(id+"F18.opExtrude","CAP_EDGE",EDGE,{"disambiguationData":[OSD([sQuery(id+"F16.wireOp",EDGE,"E88")])],"isStart":true})});
            var Q77;
            Q77=makeQuery(id+"F18.boolean.opBoolean","COPY",EDGE,{"derivedFrom":makeQuery(id+"F18.opExtrude","CAP_EDGE",EDGE,{"disambiguationData":[OSD([sQuery(id+"F16.wireOp",EDGE,"E87")])],"isStart":true})});
            var Q78;
            Q78=makeQuery(id+"F18.boolean.opBoolean","COPY",EDGE,{"derivedFrom":makeQuery(id+"F18.opExtrude","CAP_EDGE",EDGE,{"disambiguationData":[OSD([sQuery(id+"F16.wireOp",EDGE,"E89")])],"isStart":true})});
            var Q79;
            Q79=makeQuery(id+"F18.boolean.opBoolean","COPY",EDGE,{"derivedFrom":makeQuery(id+"F18.opExtrude","CAP_EDGE",EDGE,{"disambiguationData":[OSD([sQuery(id+"F16.wireOp",EDGE,"E90")])],"isStart":true})});
            var Q80;
            Q80=makeQuery(id+"F18.boolean.opBoolean","COPY",EDGE,{"derivedFrom":makeQuery(id+"F18.opExtrude","CAP_EDGE",EDGE,{"disambiguationData":[OSD([sQuery(id+"F16.wireOp",EDGE,"E96")])],"isStart":true})});
            var Q81;
            Q81=makeQuery(id+"F18.boolean.opBoolean","COPY",EDGE,{"derivedFrom":makeQuery(id+"F18.opExtrude","CAP_EDGE",EDGE,{"disambiguationData":[OSD([sQuery(id+"F16.wireOp",EDGE,"E95")])],"isStart":true})});
            var Q82;
            Q82=makeQuery(id+"F18.boolean.opBoolean","COPY",EDGE,{"derivedFrom":makeQuery(id+"F18.opExtrude","CAP_EDGE",EDGE,{"disambiguationData":[OSD([sQuery(id+"F16.wireOp",EDGE,"E66")])],"isStart":true})});
            fillet(context, id + "F19", {"entities" : qUnion([Q0, Q1, Q2, Q3, Q4, Q5, Q6, Q7, Q8, Q9, Q10, Q11, Q12, Q13, Q14, Q15, Q16, Q17, Q18, Q19, Q20, Q21, Q22, Q23, Q24, Q25, Q26, Q27, Q28, Q29, Q30, Q31, Q32, Q33, Q34, Q35, Q36, Q37, Q38, Q39, Q40, Q41, Q42, Q43, Q44, Q45, Q46, Q47, Q48, Q49, Q50, Q51, Q52, Q53, Q54, Q55, Q56, Q57, Q58, Q59, Q60, Q61, Q62, Q63, Q64, Q65, Q66, Q67, Q68, Q69, Q70, Q71, Q72, Q73, Q74, Q75, Q76, Q77, Q78, Q79, Q80, Q81, Q82]), "radius" : .3 * mm, "tangentPropagation" : true, "allowEdgeOverflow" : false});
        }
    });
